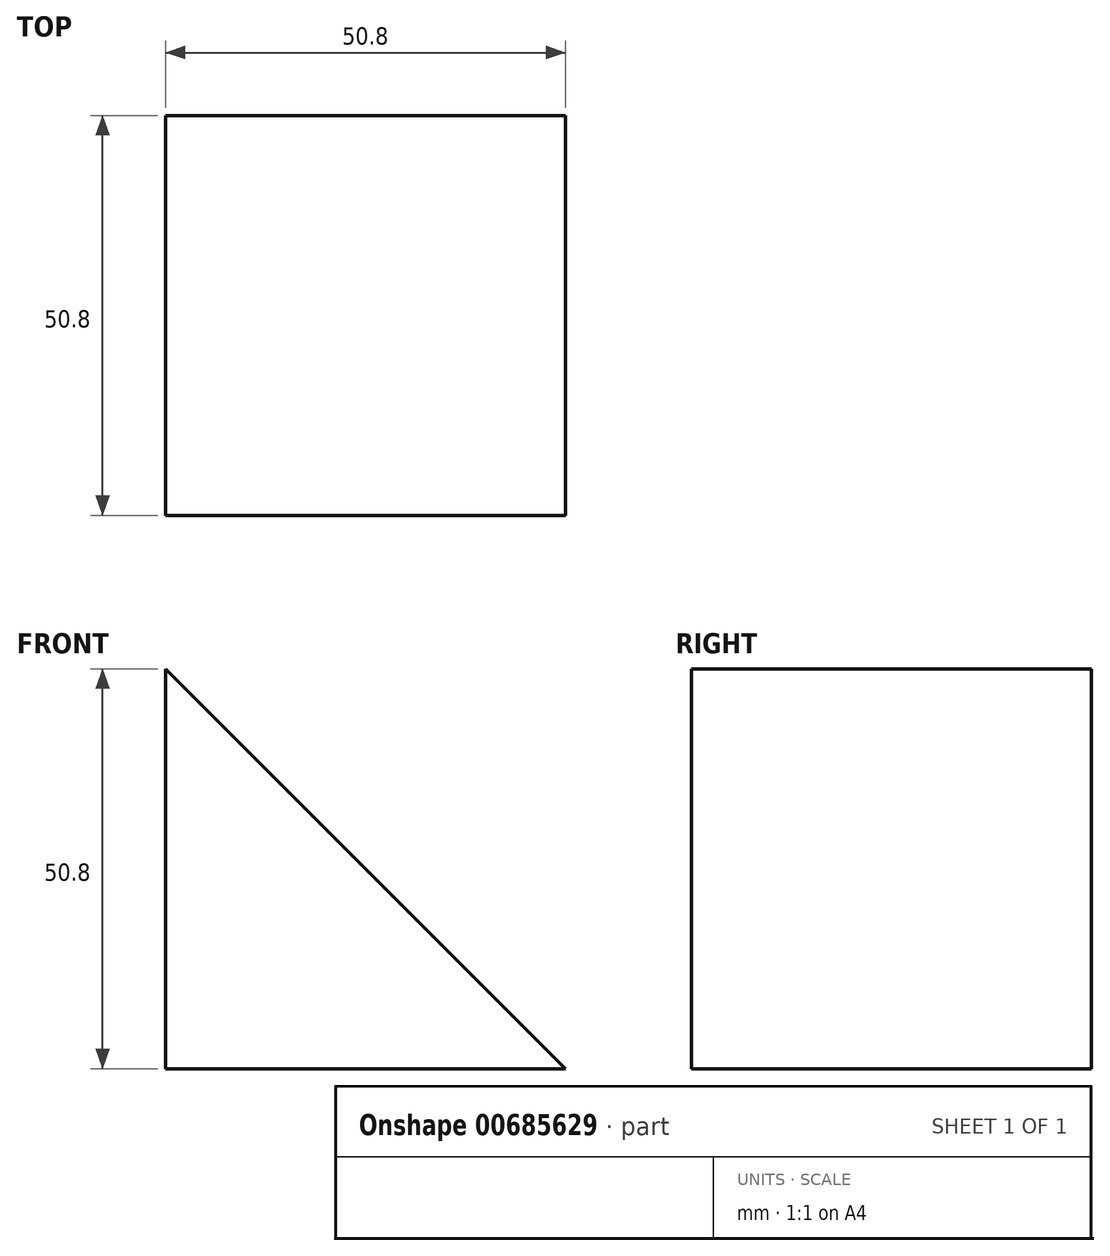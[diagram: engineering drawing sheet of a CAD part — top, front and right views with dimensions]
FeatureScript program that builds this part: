
annotation { "Feature Type Name" : "Feature", "Feature Type Description" : "" }
export const myFeature = defineFeature(function(context is Context, id is Id, definition is map)
    precondition{}
    {
        {
            var Q0;
            Q0=qCreatedBy(makeId("Front.planeOp"),FACE);
            var sketch = newSketch(context, id + "F0", { "sketchPlane" : qUnion([Q0])});
            skLineSegment(sketch, "E0", {"start": v(-50.47, 46.96) * mm, "end": v(-50.47, -3.84) * mm});
            skLineSegment(sketch, "E1", {"start": v(-50.47, -3.84) * mm, "end": v(0.33, -3.84) * mm});
            skLineSegment(sketch, "E2", {"start": v(0.33, -3.84) * mm, "end": v(-50.47, 46.96) * mm});
            skSolve(sketch);
        }
        {
            var Q0;
            Q0 = qSketchRegion(id + "F0", true);
            extrude(context, id + "F1", {"entities" : qUnion([Q0]), "depth" : 50.8 * mm, "offsetDistance" : 25.4 * mm});
        }
    });
